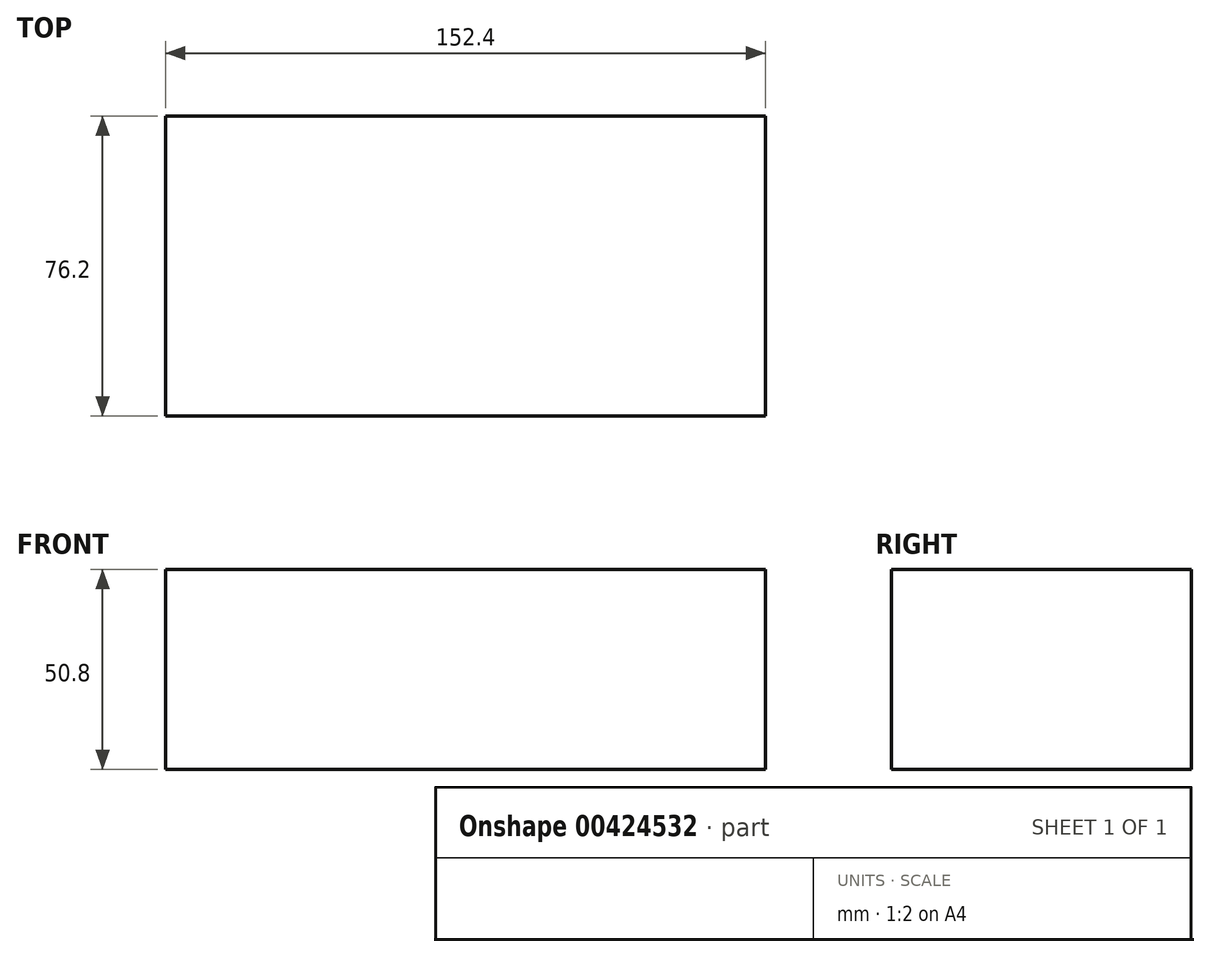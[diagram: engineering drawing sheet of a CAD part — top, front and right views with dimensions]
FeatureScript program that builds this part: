
annotation { "Feature Type Name" : "Feature", "Feature Type Description" : "" }
export const myFeature = defineFeature(function(context is Context, id is Id, definition is map)
    precondition{}
    {
        {
            var Q0;
            Q0=qCreatedBy(makeId("Front.planeOp"),FACE);
            var sketch = newSketch(context, id + "F0", { "sketchPlane" : qUnion([Q0])});
            skLineSegment(sketch, "E0", {"start": v(0, 0) * mm, "end": v(0, 50.8) * mm});
            skLineSegment(sketch, "E1", {"start": v(0, 50.8) * mm, "end": v(152.4, 50.8) * mm});
            skLineSegment(sketch, "E2", {"start": v(152.4, 50.8) * mm, "end": v(152.4, 0) * mm});
            skLineSegment(sketch, "E3", {"start": v(152.4, 0) * mm, "end": v(0, 0) * mm});
            skSolve(sketch);
        }
        {
            var Q0;
            Q0=makeQuery(id+"F0.imprint","IMPRINT",FACE,{"disambiguationData":[TD([[makeQuery(id+"F0.imprint","IMPRINT",EDGE,{"derivedFrom":sQuery(id+"F0.wireOp",EDGE,"E0")}),-1.0]])]});
            extrude(context, id + "F1", {"entities" : qUnion([Q0]), "depth" : 76.2 * mm});
        }
    });
